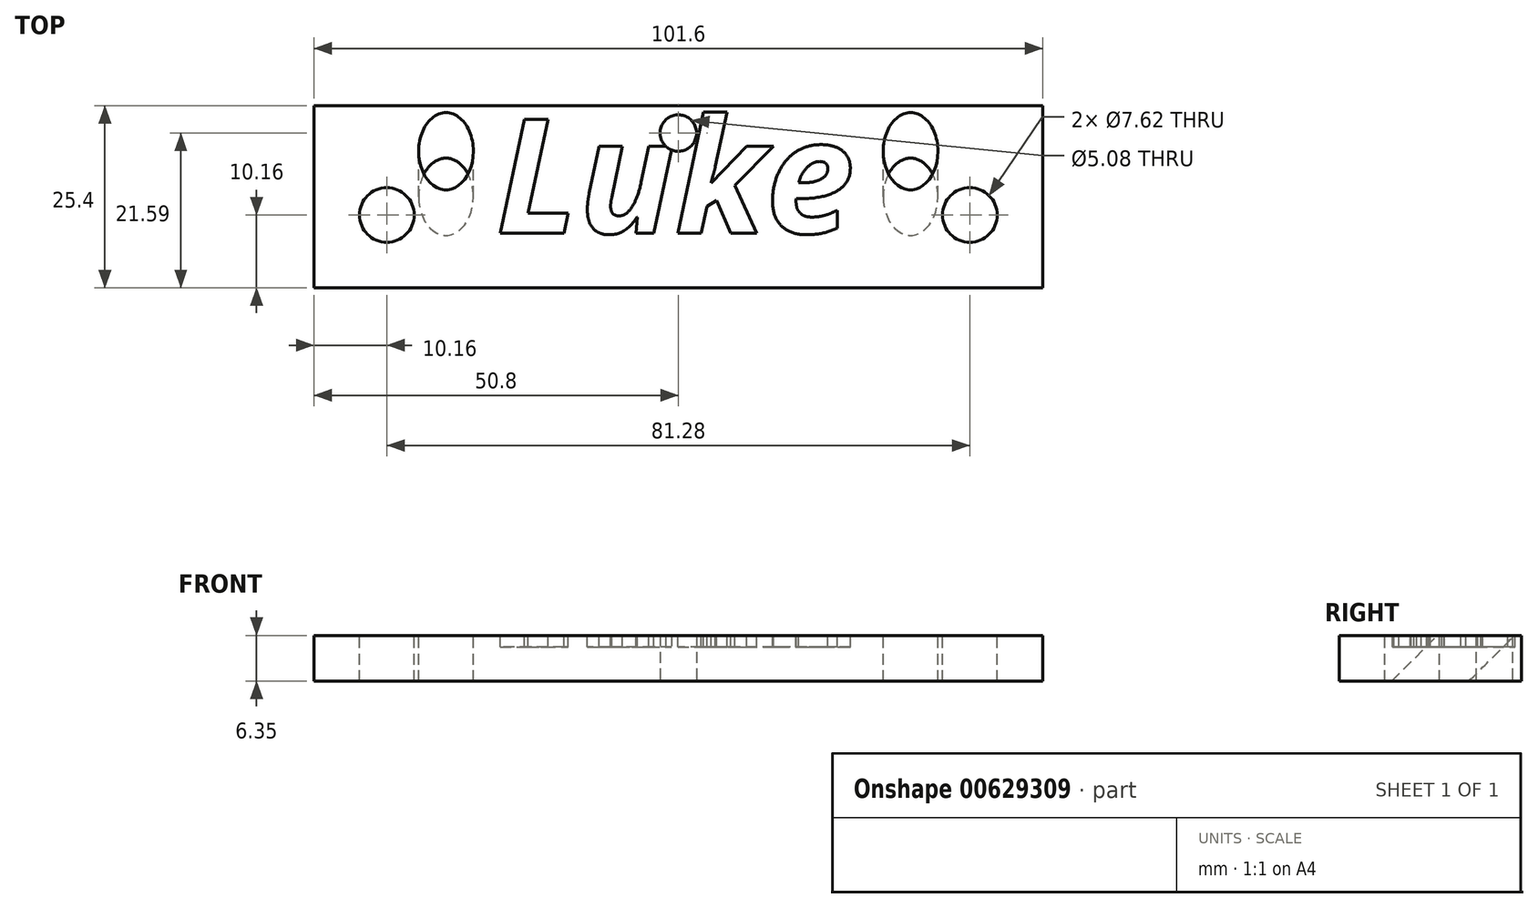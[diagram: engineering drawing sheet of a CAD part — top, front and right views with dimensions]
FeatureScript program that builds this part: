
annotation { "Feature Type Name" : "Feature", "Feature Type Description" : "" }
export const myFeature = defineFeature(function(context is Context, id is Id, definition is map)
    precondition{}
    {
        {
            var Q0;
            Q0=qCreatedBy(makeId("Top.planeOp"),FACE);
            var sketch = newSketch(context, id + "F0", { "sketchPlane" : qUnion([Q0])});
            skLineSegment(sketch, "E0.bottom", {"start": v(-50.8, -12.7) * mm, "end": v(50.8, -12.7) * mm});
            skLineSegment(sketch, "E0.top", {"start": v(-50.8, 12.7) * mm, "end": v(50.8, 12.7) * mm});
            skLineSegment(sketch, "E0.left", {"start": v(-50.8, -12.7) * mm, "end": v(-50.8, 12.7) * mm});
            skLineSegment(sketch, "E0.right", {"start": v(50.8, -12.7) * mm, "end": v(50.8, 12.7) * mm});
            skSolve(sketch);
        }
        {
            var Q0;
            Q0=qSketchRegion(id+"F0",true);
            extrude(context, id + "F1", {"entities" : qUnion([Q0]), "depth" : 6.35 * mm, "offsetDistance" : 25.4 * mm});
        }
        {
            var Q0;
            Q0=makeQuery(id+"F1.opExtrude","CAP_FACE",FACE,{"disambiguationData":[OSD([sQuery(id+"F0.wireOp",EDGE,"E0.bottom"),sQuery(id+"F0.wireOp",EDGE,"E0.top"),sQuery(id+"F0.wireOp",EDGE,"E0.left"),sQuery(id+"F0.wireOp",EDGE,"E0.right")])],"isStart":false});
            var sketch = newSketch(context, id + "F2", { "sketchPlane" : qUnion([Q0])});
            skCircle(sketch, "E1", {"center": v(-40.64, -2.54) * mm, "radius": 3.81 * mm});
            skCircle(sketch, "E2", {"center": v(40.64, -2.54) * mm, "radius": 3.81 * mm});
            skSolve(sketch);
        }
        {
            var Q0;
            Q0=makeQuery(id+"F2.imprint","IMPRINT",FACE,{"disambiguationData":[TD([[makeQuery(id+"F2.imprint","IMPRINT",EDGE,{"derivedFrom":sQuery(id+"F2.wireOp",EDGE,"E1")}),1.0]])]});
            var Q1;
            Q1=makeQuery(id+"F2.imprint","IMPRINT",FACE,{"disambiguationData":[TD([[makeQuery(id+"F2.imprint","IMPRINT",EDGE,{"derivedFrom":sQuery(id+"F2.wireOp",EDGE,"E2")}),1.0]])]});
            extrude(context, id + "F3", {"entities" : qUnion([Q0, Q1]), "operationType" : NewBodyOperationType.REMOVE, "oppositeDirection" : true, "depth" : 25.4 * mm, "offsetDistance" : 25.4 * mm});
        }
        {
            var Q0;
            Q0=qCreatedBy(makeId("Front.planeOp"),FACE);
            var sketch = newSketch(context, id + "F4", { "sketchPlane" : qUnion([Q0])});
            skPoint(sketch, "E3", {"position": v(-76.2, 76.2) * mm});
            skPoint(sketch, "E4.MirrorP", {"position": v(76.2, 76.2) * mm});
            skSolve(sketch);
        }
        {
            var Q0;
            Q0=qCreatedBy(makeId("Top.planeOp"),FACE);
            var sketch = newSketch(context, id + "F5", { "sketchPlane" : qUnion([Q0])});
            skPoint(sketch, "E5", {"position": v(0, 76.2) * mm});
            skSolve(sketch);
        }
        {
            var Q0;
            Q0=sQuery(id+"F5.wireOp",VERTEX,"E5");
            var Q1;
            Q1=sQuery(id+"F4.wireOp",VERTEX,"E3");
            var Q2;
            Q2=sQuery(id+"F4.wireOp",VERTEX,"E4.MirrorP");
            cPlane(context, id + "F6", {"entities" : qUnion([Q0, Q1, Q2]), "cplaneType" : CPlaneType.THREE_POINT, "offset" : 25.4 * mm, "width" : 152.4 * mm, "height" : 152.4 * mm});
        }
        {
            var Q0;
            Q0=qCreatedBy(id+"F6.planeOp",FACE);
            var sketch = newSketch(context, id + "F7", { "sketchPlane" : qUnion([Q0])});
            skCircle(sketch, "E6", {"center": v(-32.39, 0) * mm, "radius": 3.81 * mm});
            skCircle(sketch, "E7", {"center": v(32.39, 0) * mm, "radius": 3.81 * mm});
            skSolve(sketch);
        }
        {
            var Q0;
            Q0=makeQuery(id+"F7.imprint","IMPRINT",FACE,{"disambiguationData":[TD([[makeQuery(id+"F7.imprint","IMPRINT",EDGE,{"derivedFrom":sQuery(id+"F7.wireOp",EDGE,"E6")}),1.0]])]});
            var Q1;
            Q1=makeQuery(id+"F7.imprint","IMPRINT",FACE,{"disambiguationData":[TD([[makeQuery(id+"F7.imprint","IMPRINT",EDGE,{"derivedFrom":sQuery(id+"F7.wireOp",EDGE,"E7")}),1.0]])]});
            extrude(context, id + "F8", {"entities" : qUnion([Q0, Q1]), "operationType" : NewBodyOperationType.REMOVE, "endBound" : BoundingType.THROUGH_ALL, "depth" : 25.4 * mm, "offsetDistance" : 25.4 * mm});
        }
        {
            var Q0;
            Q0=makeQuery(id+"F1.opExtrude","CAP_FACE",FACE,{"disambiguationData":[OSD([sQuery(id+"F0.wireOp",EDGE,"E0.bottom"),sQuery(id+"F0.wireOp",EDGE,"E0.top"),sQuery(id+"F0.wireOp",EDGE,"E0.left"),sQuery(id+"F0.wireOp",EDGE,"E0.right")])],"isStart":false});
            var sketch = newSketch(context, id + "F9", { "sketchPlane" : qUnion([Q0])});
            skText(sketch, "E8", { "text": "Luke", "fontName": "OpenSans-BoldItalic.ttf"});
            const initialGuessF9  = {"E8": [-0.0254, -0.00508, 1, 0, 0.016]};
            skSetInitialGuess(sketch, initialGuessF9);
            skSolve(sketch);
        }
        {
            var Q0;
            Q0=qSketchRegion(id+"F9",true);
            extrude(context, id + "F10", {"entities" : qUnion([Q0]), "operationType" : NewBodyOperationType.REMOVE, "oppositeDirection" : true, "depth" : 1.59 * mm, "offsetDistance" : 25.4 * mm});
        }
        {
            var Q0;
            Q0=makeQuery(id+"F1.opExtrude","CAP_FACE",FACE,{"disambiguationData":[OSD([sQuery(id+"F0.wireOp",EDGE,"E0.bottom"),sQuery(id+"F0.wireOp",EDGE,"E0.top"),sQuery(id+"F0.wireOp",EDGE,"E0.left"),sQuery(id+"F0.wireOp",EDGE,"E0.right")])],"isStart":true});
            var sketch = newSketch(context, id + "F11", { "sketchPlane" : qUnion([Q0])});
            skCircle(sketch, "E9", {"center": v(0, -8.9) * mm, "radius": 2.54 * mm});
            skSolve(sketch);
        }
        {
            var Q0;
            Q0=makeQuery(id+"F11.imprint","IMPRINT",FACE,{"disambiguationData":[TD([[makeQuery(id+"F11.imprint","IMPRINT",EDGE,{"derivedFrom":sQuery(id+"F11.wireOp",EDGE,"E9")}),1.0]])]});
            extrude(context, id + "F12", {"entities" : qUnion([Q0]), "operationType" : NewBodyOperationType.REMOVE, "oppositeDirection" : true, "depth" : 25.4 * mm, "offsetDistance" : 25.4 * mm});
        }
    });
